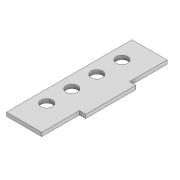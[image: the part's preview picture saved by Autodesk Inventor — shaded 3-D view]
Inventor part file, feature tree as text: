
AUTODESK INVENTOR PART (.ipt)
format: ipt  version: 2020 (Build 240168000, 168)  size: 109,056 bytes
history: native  units: mm
features: extrude x2, sketch x2
ambient origin geometry x8: Origin, YZ Plane, XZ Plane, XY Plane, X Axis, Y Axis, Z Axis, Center Point
bodies: Solid1 (feature_tree)
feature tree (4):
  extrude  "Extrusion1"  Depth=5.0mm
  extrude  "Extrusion2"  Depth=28.0mm
  sketch  "Sketch1"  dims[d0=100.0mm d1=5.0mm]
  sketch  "Sketch2"  dims[d2=40.0mm d3=28.0mm d4=3.0mm d5=0.0mm d6=9.2mm d7=18.0mm d8=22.0mm d9=40.0mm d11=20.0mm d12=10.0mm d14=10.0mm d16=5.0mm d17=0.0mm]
